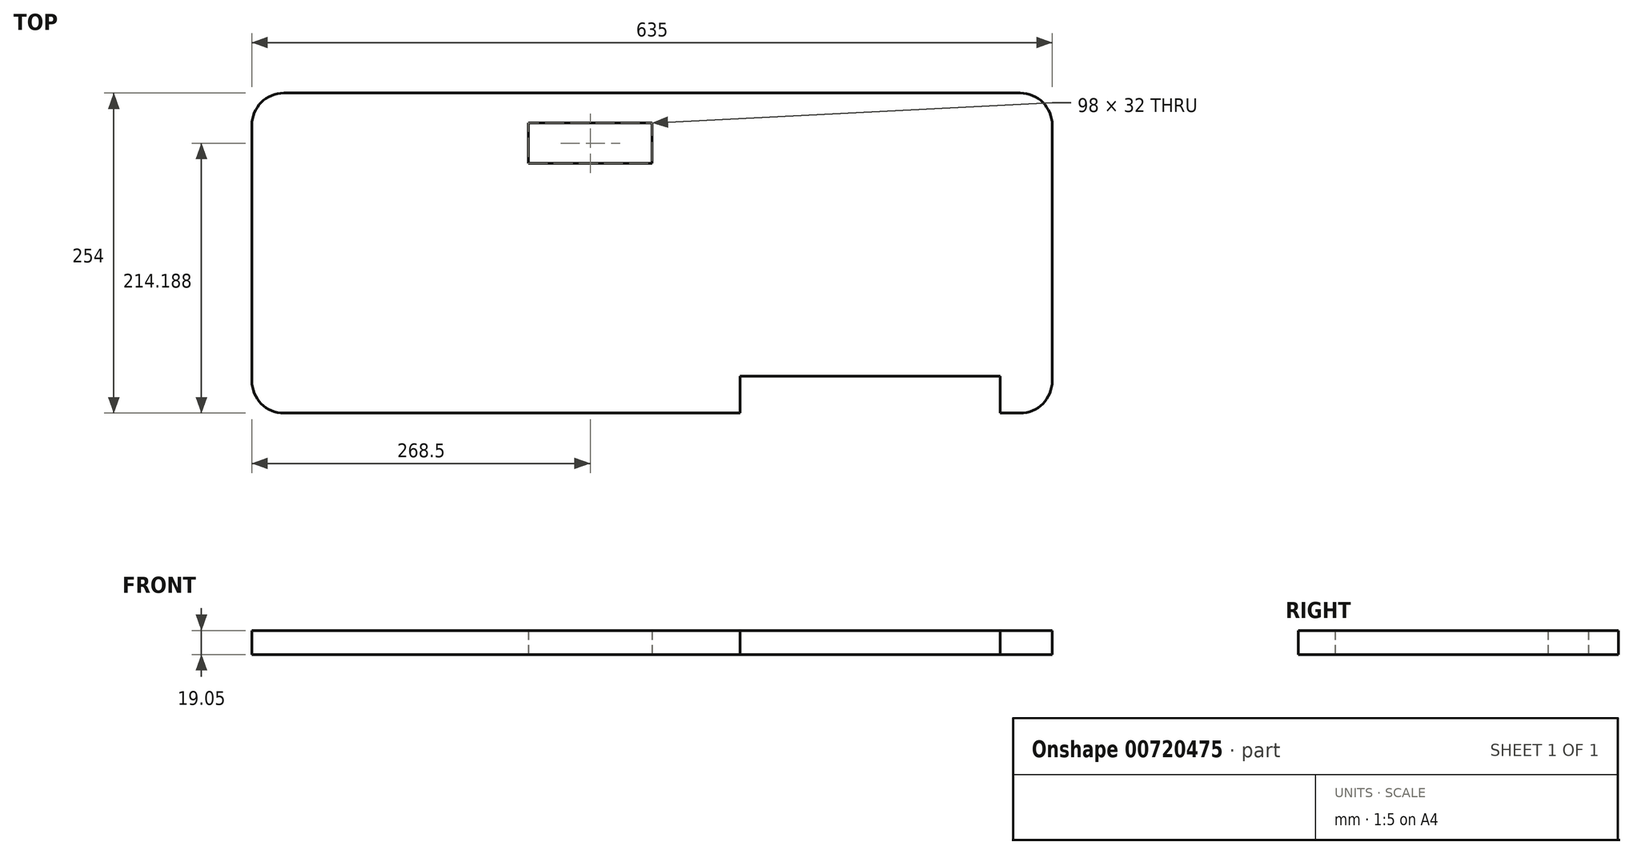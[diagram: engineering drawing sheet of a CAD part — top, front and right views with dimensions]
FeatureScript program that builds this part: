
annotation { "Feature Type Name" : "Feature", "Feature Type Description" : "" }
export const myFeature = defineFeature(function(context is Context, id is Id, definition is map)
    precondition{}
    {
        {
            var Q0;
            Q0=qCreatedBy(makeId("Top.planeOp"),FACE);
            var sketch = newSketch(context, id + "F0", { "sketchPlane" : qUnion([Q0])});
            skLineSegment(sketch, "E0.bottom", {"start": v(292.1, -127) * mm, "end": v(-292.1, -127) * mm});
            skLineSegment(sketch, "E0.top", {"start": v(292.1, 127) * mm, "end": v(-292.1, 127) * mm});
            skLineSegment(sketch, "E0.left", {"start": v(317.5, -101.6) * mm, "end": v(317.5, 101.6) * mm});
            skLineSegment(sketch, "E0.right", {"start": v(-317.5, -101.6) * mm, "end": v(-317.5, 101.6) * mm});
            skLineSegment(sketch, "E1.bottom", {"start": v(69.85, 103.19) * mm, "end": v(276.22, 103.19) * mm});
            skLineSegment(sketch, "E1.top", {"start": v(69.85, -107.95) * mm, "end": v(276.22, -107.95) * mm});
            skLineSegment(sketch, "E1.left", {"start": v(47.62, 80.96) * mm, "end": v(47.62, -85.72) * mm});
            skLineSegment(sketch, "E1.right", {"start": v(298.45, 80.96) * mm, "end": v(298.45, -85.72) * mm});
            skPoint(sketch, "E2.visualSharp", {"position": v(47.63, 103.19) * mm});
            skArc(sketch, "E2.filletArc", {"start": v(69.85, 103.19) * mm, "mid": v(54.13, 96.68) * mm, "end": v(47.62, 80.96) * mm});
            skPoint(sketch, "E3.visualSharp", {"position": v(298.45, 103.19) * mm});
            skArc(sketch, "E3.filletArc", {"start": v(298.45, 80.96) * mm, "mid": v(291.94, 96.68) * mm, "end": v(276.22, 103.19) * mm});
            skPoint(sketch, "E4.visualSharp", {"position": v(298.45, -107.95) * mm});
            skArc(sketch, "E4.filletArc", {"start": v(276.22, -107.95) * mm, "mid": v(291.94, -101.44) * mm, "end": v(298.45, -85.72) * mm});
            skPoint(sketch, "E5.visualSharp", {"position": v(47.62, -107.95) * mm});
            skArc(sketch, "E5.filletArc", {"start": v(47.62, -85.72) * mm, "mid": v(54.13, -101.44) * mm, "end": v(69.85, -107.95) * mm});
            skPoint(sketch, "E6.visualSharp", {"position": v(-317.5, 127) * mm});
            skArc(sketch, "E6.filletArc", {"start": v(-292.1, 127) * mm, "mid": v(-310.06, 119.56) * mm, "end": v(-317.5, 101.6) * mm});
            skPoint(sketch, "E7.visualSharp", {"position": v(-317.5, -127) * mm});
            skArc(sketch, "E7.filletArc", {"start": v(-317.5, -101.6) * mm, "mid": v(-310.06, -119.56) * mm, "end": v(-292.1, -127) * mm});
            skPoint(sketch, "E8.visualSharp", {"position": v(317.5, -127) * mm});
            skArc(sketch, "E8.filletArc", {"start": v(292.1, -127) * mm, "mid": v(310.06, -119.56) * mm, "end": v(317.5, -101.6) * mm});
            skPoint(sketch, "E9.visualSharp", {"position": v(317.5, 127) * mm});
            skArc(sketch, "E9.filletArc", {"start": v(317.5, 101.6) * mm, "mid": v(310.06, 119.56) * mm, "end": v(292.1, 127) * mm});
            skLineSegment(sketch, "E10.bottom", {"start": v(69.85, -97.76) * mm, "end": v(276.22, -97.76) * mm});
            skLineSegment(sketch, "E10.top", {"start": v(69.85, -133.93) * mm, "end": v(276.22, -133.93) * mm});
            skLineSegment(sketch, "E10.left", {"start": v(69.85, -97.76) * mm, "end": v(69.85, -133.93) * mm});
            skLineSegment(sketch, "E10.right", {"start": v(276.22, -97.76) * mm, "end": v(276.22, -133.93) * mm});
            skLineSegment(sketch, "E11.bottom", {"start": v(-98, 103.19) * mm, "end": v(0, 103.19) * mm});
            skLineSegment(sketch, "E11.top", {"start": v(-98, 71.19) * mm, "end": v(0, 71.19) * mm});
            skLineSegment(sketch, "E11.left", {"start": v(-98, 103.19) * mm, "end": v(-98, 71.19) * mm});
            skLineSegment(sketch, "E11.right", {"start": v(0, 103.19) * mm, "end": v(0, 71.19) * mm});
            skSolve(sketch);
        }
        {
            var Q0;
            Q0=makeQuery(id+"F0.imprint","IMPRINT",FACE,{"disambiguationData":[TD([[makeQuery(id+"F0.imprint","IMPRINT",EDGE,{"derivedFrom":sQuery(id+"F0.wireOp",EDGE,"E0.bottom")}),-1.0]])]});
            var Q1;
            Q1=makeQuery(id+"F0.imprint","IMPRINT",FACE,{"disambiguationData":[TD([[makeQuery(id+"F0.imprint","IMPRINT",EDGE,{"derivedFrom":sQuery(id+"F0.wireOp",EDGE,"E1.bottom")}),-1.0]])]});
            extrude(context, id + "F1", {"entities" : qUnion([Q0, Q1]), "depth" : 19.05 * mm, "offsetDistance" : 25.4 * mm});
        }
    });
